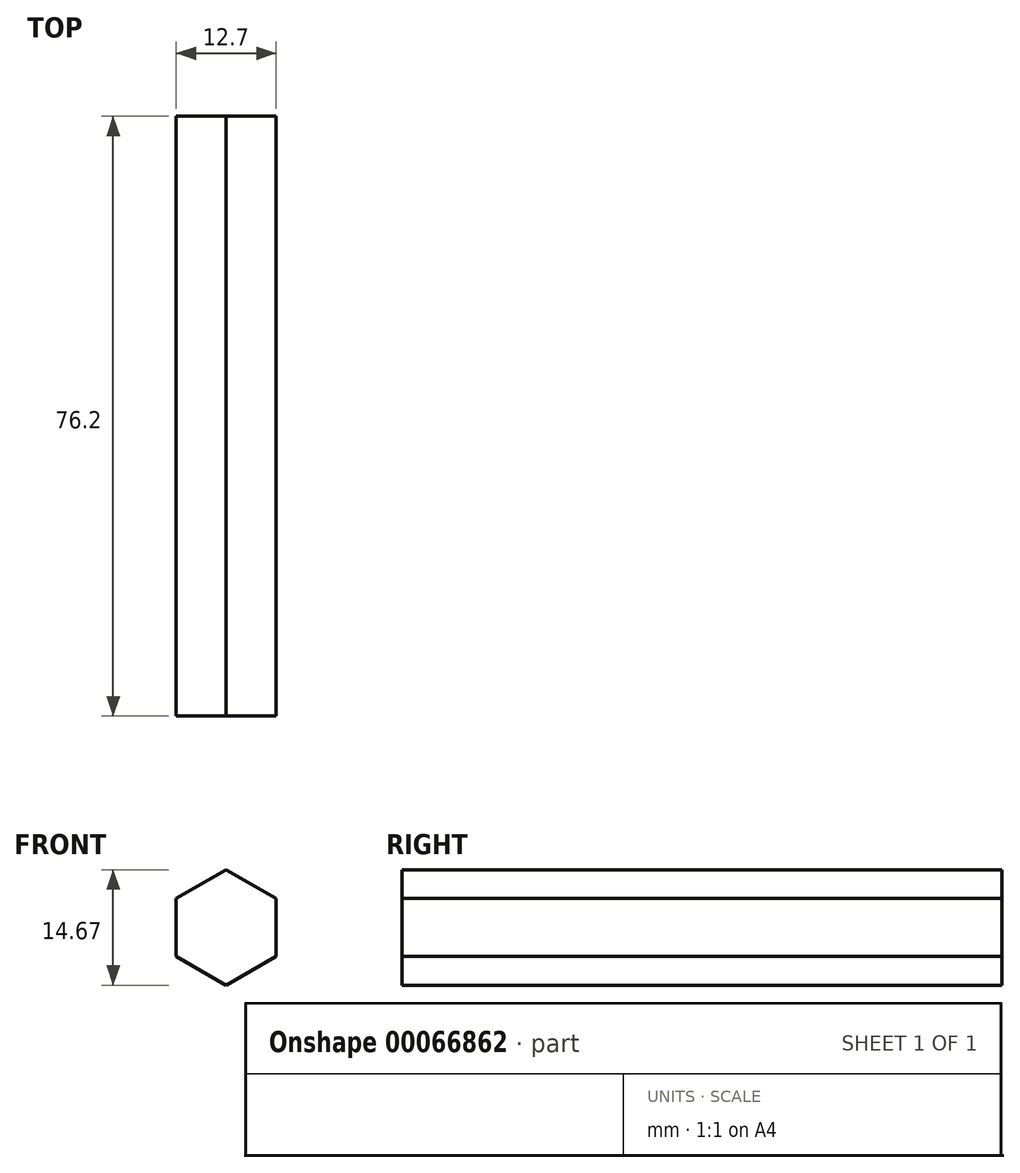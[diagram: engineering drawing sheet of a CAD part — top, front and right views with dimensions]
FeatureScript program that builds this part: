
annotation { "Feature Type Name" : "Feature", "Feature Type Description" : "" }
export const myFeature = defineFeature(function(context is Context, id is Id, definition is map)
    precondition{}
    {
        {
            var Q0;
            Q0=qCreatedBy(makeId("Front.planeOp"),FACE);
            var sketch = newSketch(context, id + "F0", { "sketchPlane" : qUnion([Q0])});
            skCircle(sketch, "E0.cCircle", {"center": v(-15.5, 20.9) * mm, "radius": 6.35 * mm, "construction": true});
            skLineSegment(sketch, "E0.0", {"start": v(-9.14, 24.56) * mm, "end": v(-9.14, 17.23) * mm});
            skLineSegment(sketch, "E0.1", {"start": v(-9.14, 17.23) * mm, "end": v(-15.5, 13.56) * mm});
            skLineSegment(sketch, "E0.2", {"start": v(-15.5, 13.56) * mm, "end": v(-21.84, 17.23) * mm});
            skLineSegment(sketch, "E0.3", {"start": v(-21.84, 17.23) * mm, "end": v(-21.84, 24.56) * mm});
            skLineSegment(sketch, "E0.4", {"start": v(-21.84, 24.56) * mm, "end": v(-15.5, 28.23) * mm});
            skLineSegment(sketch, "E0.5", {"start": v(-15.5, 28.23) * mm, "end": v(-9.14, 24.56) * mm});
            skPoint(sketch, "E0.0.midPoint", {"position": v(-9.14, 20.9) * mm});
            skSolve(sketch);
        }
        {
            var Q0;
            Q0=makeQuery(id+"F0.imprint","IMPRINT",FACE,{"disambiguationData":[TD([[makeQuery(id+"F0.imprint","IMPRINT",EDGE,{"derivedFrom":sQuery(id+"F0.wireOp",EDGE,"E0.0")}),-1.0]])]});
            extrude(context, id + "F1", {"entities" : qUnion([Q0]), "depth" : 76.2 * mm});
        }
    });
